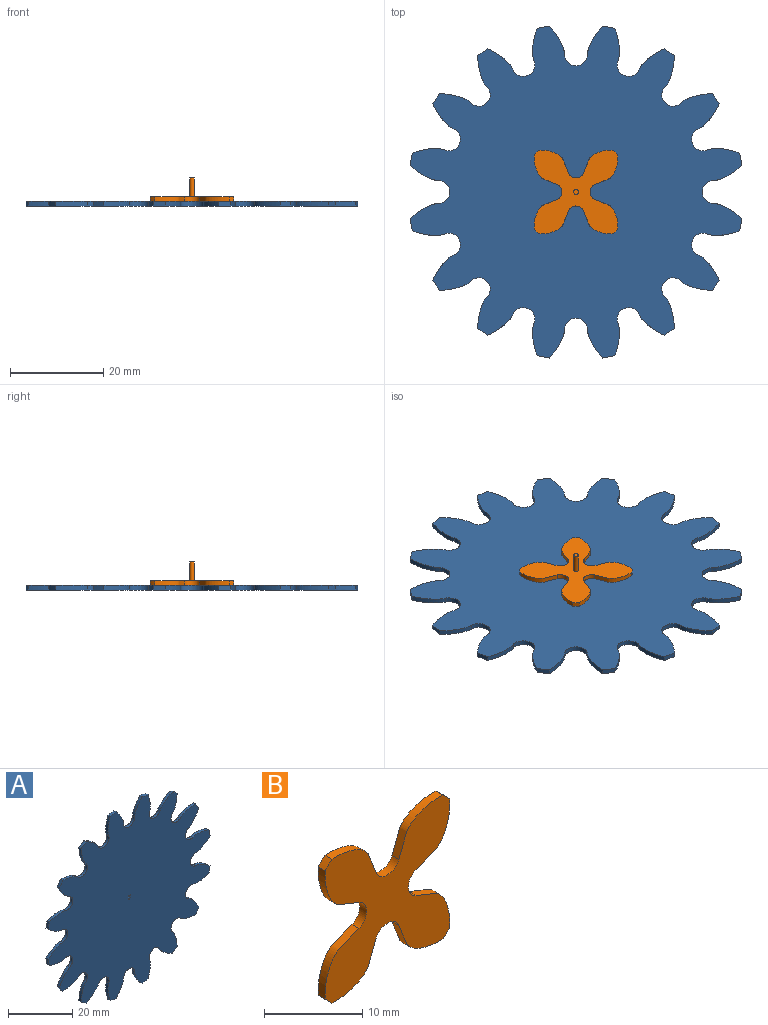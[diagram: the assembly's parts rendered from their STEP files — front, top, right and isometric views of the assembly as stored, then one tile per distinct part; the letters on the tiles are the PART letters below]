
ASSEMBLY  parts=2 mates=1
PART A: 70 faces, bbox 71.1x1x71.1 mm
  f0: cylinder r=36mm len=2.21mm, axis (0,1,0), area 2.7mm2, adj f15,f16,f64,f68
  f1: cylinder r=36mm len=2.61mm, axis (0,1,0), area 2.7mm2, adj f15,f16,f49,f65
  f2: cylinder r=36mm len=2.21mm, axis (0,1,0), area 2.7mm2, adj f15,f16,f62,f67
  f3: cylinder r=36mm len=2.21mm, axis (0,1,0), area 2.7mm2, adj f15,f16,f55,f59
  f4: cylinder r=36mm len=2.61mm, axis (0,1,0), area 2.7mm2, adj f15,f16,f37,f56
  f5: cylinder r=36mm len=2.21mm, axis (0,1,0), area 2.7mm2, adj f15,f16,f53,f58
  f6: cylinder r=36mm len=2.61mm, axis (0,1,0), area 2.7mm2, adj f15,f16,f50,f52
  f7: cylinder r=36mm len=2.21mm, axis (0,1,0), area 2.7mm2, adj f15,f16,f43,f47
  f8: cylinder r=36mm len=2.61mm, axis (0,1,0), area 2.7mm2, adj f15,f16,f25,f44
  f9: cylinder r=36mm len=2.21mm, axis (0,1,0), area 2.7mm2, adj f15,f16,f41,f46
  f10: cylinder r=36mm len=2.61mm, axis (0,1,0), area 2.7mm2, adj f15,f16,f38,f40
  f11: cylinder r=36mm len=2.21mm, axis (0,1,0), area 2.7mm2, adj f15,f16,f31,f35
  f12: cylinder r=36mm len=2.61mm, axis (0,1,0), area 2.7mm2, adj f15,f16,f22,f32
  f13: cylinder r=36mm len=2.21mm, axis (0,1,0), area 2.7mm2, adj f15,f16,f29,f34
  f14: cylinder r=36mm len=2.61mm, axis (0,1,0), area 2.7mm2, adj f15,f16,f26,f28
  f15: plane 71.12x71.12mm, normal (0,-1,0), area 3148.6mm2, adj f0,f1,f2,f3,f4,f5,f6,f7
  f16: plane 71.12x71.12mm, normal (0,1,0), area 3148.6mm2, adj f0,f1,f2,f3,f4,f5,f6,f7
  f17: cylinder r=0.5mm len=1mm, axis (0,1,0), area 1.6mm2, adj f15,f16,f18,f20
  f18: plane 1x1mm, normal (1,0,0), area 1mm2, adj f15,f16,f17,f19
  f19: plane 1x1mm, normal (0,0,-1), area 1mm2, adj f15,f16,f18,f20
  f20: plane 1x1mm, normal (-1,0,0), area 1mm2, adj f15,f16,f17,f19
  f21: cylinder r=36mm len=2.61mm, axis (0,1,0), area 2.7mm2, adj f15,f16,f23,f61
  f22: extruded ~6.31x3.28mm, area 7.2mm2, adj f12,f15,f16,f24
  f23: extruded ~6.31x3.28mm, area 7.2mm2, adj f15,f16,f21,f24
  f24: cylinder r=2.44mm len=4.87mm, axis (0,1,0), area 7.3mm2, adj f15,f16,f22,f23
  f25: extruded ~6.31x3.28mm, area 7.2mm2, adj f8,f15,f16,f27
  f26: extruded ~6.31x3.28mm, area 7.2mm2, adj f14,f15,f16,f27
  f27: cylinder r=2.44mm len=4.87mm, axis (0,1,0), area 7.3mm2, adj f15,f16,f25,f26
  f28: extruded ~7.08x1mm, area 7.2mm2, adj f14,f15,f16,f30
  f29: extruded ~5.44x4.57mm, area 7.2mm2, adj f13,f15,f16,f30
  f30: cylinder r=2.44mm len=4.62mm, axis (0,1,0), area 7.3mm2, adj f15,f16,f28,f29
  f31: extruded ~5.44x4.57mm, area 7.2mm2, adj f11,f15,f16,f33
  f32: extruded ~7.08x1mm, area 7.2mm2, adj f12,f15,f16,f33
  f33: cylinder r=2.44mm len=4.62mm, axis (0,1,0), area 7.3mm2, adj f15,f16,f31,f32
  f34: extruded ~6.78x2.14mm, area 7.2mm2, adj f13,f15,f16,f36
  f35: extruded ~6.78x2.14mm, area 7.2mm2, adj f11,f15,f16,f36
  f36: cylinder r=2.44mm len=4.02mm, axis (0,1,0), area 7.3mm2, adj f15,f16,f34,f35
  f37: extruded ~6.31x3.28mm, area 7.2mm2, adj f4,f15,f16,f39
  f38: extruded ~6.31x3.28mm, area 7.2mm2, adj f10,f15,f16,f39
  f39: cylinder r=2.44mm len=4.87mm, axis (0,1,0), area 7.3mm2, adj f15,f16,f37,f38
  f40: extruded ~7.08x1mm, area 7.2mm2, adj f10,f15,f16,f42
  f41: extruded ~5.44x4.57mm, area 7.2mm2, adj f9,f15,f16,f42
  f42: cylinder r=2.44mm len=4.62mm, axis (0,1,0), area 7.3mm2, adj f15,f16,f40,f41
  f43: extruded ~5.44x4.57mm, area 7.2mm2, adj f7,f15,f16,f45
  f44: extruded ~7.08x1mm, area 7.2mm2, adj f8,f15,f16,f45
  f45: cylinder r=2.44mm len=4.62mm, axis (0,1,0), area 7.3mm2, adj f15,f16,f43,f44
  f46: extruded ~6.78x2.14mm, area 7.2mm2, adj f9,f15,f16,f48
  f47: extruded ~6.78x2.14mm, area 7.2mm2, adj f7,f15,f16,f48
  f48: cylinder r=2.44mm len=4.02mm, axis (0,1,0), area 7.3mm2, adj f15,f16,f46,f47
  f49: extruded ~6.31x3.28mm, area 7.2mm2, adj f1,f15,f16,f51
  f50: extruded ~6.31x3.28mm, area 7.2mm2, adj f6,f15,f16,f51
  f51: cylinder r=2.44mm len=4.87mm, axis (0,1,0), area 7.3mm2, adj f15,f16,f49,f50
  f52: extruded ~7.08x1mm, area 7.2mm2, adj f6,f15,f16,f54
  f53: extruded ~5.44x4.57mm, area 7.2mm2, adj f5,f15,f16,f54
  f54: cylinder r=2.44mm len=4.62mm, axis (0,1,0), area 7.3mm2, adj f15,f16,f52,f53
  f55: extruded ~5.44x4.57mm, area 7.2mm2, adj f3,f15,f16,f57
  f56: extruded ~7.08x1mm, area 7.2mm2, adj f4,f15,f16,f57
  f57: cylinder r=2.44mm len=4.62mm, axis (0,1,0), area 7.3mm2, adj f15,f16,f55,f56
  f58: extruded ~6.78x2.14mm, area 7.2mm2, adj f5,f15,f16,f60
  f59: extruded ~6.78x2.14mm, area 7.2mm2, adj f3,f15,f16,f60
  f60: cylinder r=2.44mm len=4.02mm, axis (0,1,0), area 7.3mm2, adj f15,f16,f58,f59
  f61: extruded ~7.08x1mm, area 7.2mm2, adj f15,f16,f21,f63
  f62: extruded ~5.44x4.57mm, area 7.2mm2, adj f2,f15,f16,f63
  f63: cylinder r=2.44mm len=4.62mm, axis (0,1,0), area 7.3mm2, adj f15,f16,f61,f62
  f64: extruded ~5.44x4.57mm, area 7.2mm2, adj f0,f15,f16,f66
  f65: extruded ~7.08x1mm, area 7.2mm2, adj f1,f15,f16,f66
  f66: cylinder r=2.44mm len=4.62mm, axis (0,1,0), area 7.3mm2, adj f15,f16,f64,f65
  f67: extruded ~6.78x2.14mm, area 7.2mm2, adj f2,f15,f16,f69
  f68: extruded ~6.78x2.14mm, area 7.2mm2, adj f0,f15,f16,f69
  f69: cylinder r=2.44mm len=4.02mm, axis (0,1,0), area 7.3mm2, adj f15,f16,f67,f68
PART B: 20 faces, bbox 17.9x5x17.9 mm
  f0: cylinder r=12mm len=1mm, axis (0,1,0), area 1.4mm2, adj f3,f4,f12,f16
  f1: cylinder r=12mm len=1mm, axis (0,1,0), area 1.4mm2, adj f3,f4,f6,f13
  f2: cylinder r=12mm len=1mm, axis (0,1,0), area 1.4mm2, adj f3,f4,f10,f15
  f3: plane 17.95x17.95mm, normal (0,-1,0), area 194.5mm2, adj f0,f1,f2,f5,f6,f7,f8,f9
  f4: plane 17.95x17.95mm, normal (0,1,0), area 193.7mm2, adj f0,f1,f2,f5,f6,f7,f8,f9
  f5: cylinder r=12mm len=1mm, axis (0,1,0), area 1.4mm2, adj f3,f4,f7,f9
  f6: extruded ~6.36x4.86mm, area 9mm2, adj f1,f3,f4,f8
  f7: extruded ~6.36x4.86mm, area 9mm2, adj f3,f4,f5,f8
  f8: cylinder r=1.75mm len=3.26mm, axis (0,1,0), area 4.2mm2, adj f3,f4,f6,f7
  f9: extruded ~6.36x4.86mm, area 9mm2, adj f3,f4,f5,f11
  f10: extruded ~6.36x4.86mm, area 9mm2, adj f2,f3,f4,f11
  f11: cylinder r=1.75mm len=3.26mm, axis (0,1,0), area 4.2mm2, adj f3,f4,f9,f10
  f12: extruded ~6.36x4.86mm, area 9mm2, adj f0,f3,f4,f14
  f13: extruded ~6.36x4.86mm, area 9mm2, adj f1,f3,f4,f14
  f14: cylinder r=1.75mm len=3.26mm, axis (0,1,0), area 4.2mm2, adj f3,f4,f12,f13
  f15: extruded ~6.36x4.86mm, area 9mm2, adj f2,f3,f4,f17
  f16: extruded ~6.36x4.86mm, area 9mm2, adj f0,f3,f4,f17
  f17: cylinder r=1.75mm len=3.26mm, axis (0,1,0), area 4.2mm2, adj f3,f4,f15,f16
  f18: cylinder r=0.5mm len=4mm, axis (0,-1,0), area 12.6mm2, adj f4,f19
  f19: plane 1x1mm, normal (0,1,0), area 0.8mm2, adj f18
PLACE A rot(axis=(1,0,0),90deg) t=(0,0,0)mm
PLACE B rot(axis=(0.58,-0.58,-0.58),120deg) t=(0,0,1)mm
MATE fastened A.f0 <-> B.f0  axis (0,0,1) through (0,0,0)mm
